# Revit family: HL_Трап для внутренних помещений_HL300-3020
name_source: partatom
category: Instalační zařizovací předměty
revit_build: Autodesk Revit 2016 (Build: 20151007_0715(x64)
units: mm (PartAtom-declared; Revit-internal decimal feet)

## family parameters
Bod výpočtu místnosti = Ano
Kóta kulaté spojky = Použít průměr
Nadpis OmniClass = Deck Waste Water Drains
Ořezat dutým tvarem při načtení = Ne
Sdílené = Ano
Typ součásti = Normální
Vždy vertikální = Ano
Založené na pracovní rovině = Ne
Číslo OmniClass = 23.70.50.21.24.14

## types (1)
- HL300-3020
    EAN = 9003076034345
    Klíčová poznámka = HL300-3020
    Komentáře k typům = HL300-3020 Трап для внутренний помещений с гидрозатвором и обратным клапаном, горизонтальный DN50, с дополнительным входом DN40/50, с надставным элементом для вклеивания керамической плитки 132х132/112х112 мм
    Model = HL300-3020
    Popis = Трапы для внутренних помещений
    Připojení CW = Ne
    Připojení HW = Ne
    Připojení odpadu = Ano
    Připojení ventilace = Ne
    URL = http://www.hutterer-lechner.com
    Výrobce = HL Hutterer & Lechner GmbH
    ВЕС = 0,85 [kg]
    ВЫСОТА МОНТАЖА = 155 mm
    МАКСИМАЛЬНАЯ НАГРУЗКА КЛАССА = K3 - 300 kg
    МАТЕРИАЛ = PE
    НАСАДКА = 112 x 112 mm / ABS-V4A
    НОМИНАЛЬНЫЙ ДИАМЕТР = 50 mm
    ПРИЁМНОЕ ОТВЕРСТИЕ = DN40/50
    ПРОИЗВОДИТЕЛЬНОСТЬ = 0,5 l/sec
    ПРОПУСКНАЯ СПОСОБНОСТЬ = 0.5 L/s
    РАЗМЕР = DN50
    РЕШЁТКА = 10 - 80 mm / 132 x 132 mm / PP-V4A

## geometry (parser evidence)
native form markers: Sweep x13
no freeform markers — native parametric forms only
